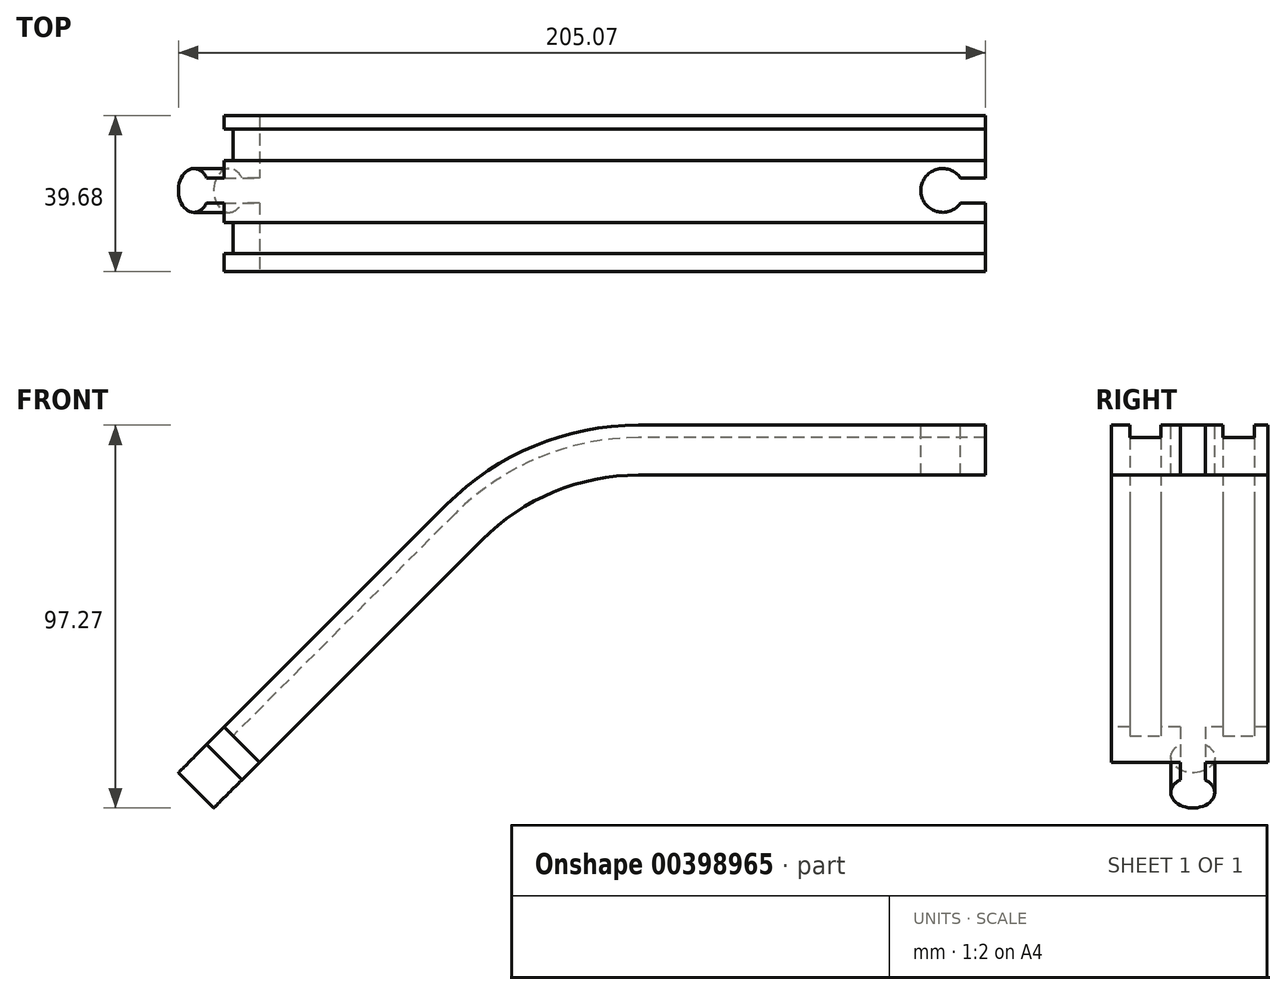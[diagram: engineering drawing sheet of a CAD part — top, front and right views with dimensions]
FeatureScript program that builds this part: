
annotation { "Feature Type Name" : "Feature", "Feature Type Description" : "" }
export const myFeature = defineFeature(function(context is Context, id is Id, definition is map)
    precondition{}
    {
        {
            var Q0;
            Q0=qCreatedBy(makeId("Right.planeOp"),FACE);
            var sketch = newSketch(context, id + "F0", { "sketchPlane" : qUnion([Q0])});
            skLineSegment(sketch, "E0.bottom", {"start": v(19.84, 6.35) * mm, "end": v(-19.84, 6.35) * mm});
            skLineSegment(sketch, "E0.top", {"start": v(19.84, -6.35) * mm, "end": v(-19.84, -6.35) * mm});
            skLineSegment(sketch, "E0.left", {"start": v(19.84, 6.35) * mm, "end": v(19.84, -6.35) * mm});
            skLineSegment(sketch, "E0.right", {"start": v(-19.84, 6.35) * mm, "end": v(-19.84, -6.35) * mm});
            skPoint(sketch, "E0.middle", {"position": v(0, 0) * mm});
            skSolve(sketch);
        }
        {
            var Q0;
            Q0=qCreatedBy(makeId("Front.planeOp"),FACE);
            var sketch = newSketch(context, id + "F1", { "sketchPlane" : qUnion([Q0])});
            skLineSegment(sketch, "E1", {"start": v(0, 0) * mm, "end": v(-88.25, 0) * mm});
            skArc(sketch, "E2", {"start": v(-88.25, 0) * mm, "mid": v(-112.17, -4.76) * mm, "end": v(-132.46, -18.31) * mm});
            skLineSegment(sketch, "E3", {"start": v(-132.46, -18.31) * mm, "end": v(-188.94, -74.79) * mm});
            skPoint(sketch, "E4", {"position": v(-132.46, -18.31) * mm});
            skSolve(sketch);
        }
        {
            var Q0;
            Q0 = qSketchRegion(id + "F0", true);
            var Q1;
            Q1 = qConstructionFilter(qBodyType(qCreatedBy(id + "F1" ,EDGE), BodyType.WIRE), ConstructionObject.NO);
            sweep(context, id + "F2", {"profiles" : qUnion([Q0]), "path" : qUnion([Q1])});
        }
        {
            var Q0;
            Q0=qCreatedBy(makeId("Top.planeOp"),FACE);
            var sketch = newSketch(context, id + "F3", { "sketchPlane" : qUnion([Q0])});
            skLineSegment(sketch, "E5.0", {"start": v(0, -19.84) * mm, "end": v(0, 19.84) * mm});
            skLineSegment(sketch, "E6", {"start": v(0, 3.97) * mm, "end": v(-6.35, 3.97) * mm});
            skLineSegment(sketch, "E7", {"start": v(0, -2.38) * mm, "end": v(-6.35, -2.38) * mm});
            skArc(sketch, "E8", {"start": v(-6.35, 3.97) * mm, "mid": v(-16.47, 0.8) * mm, "end": v(-6.35, -2.38) * mm});
            skSolve(sketch);
        }
        {
            var Q0;
            Q0 = qSketchRegion(id + "F3", true);
            extrude(context, id + "F4", {"entities" : qUnion([Q0]), "operationType" : NewBodyOperationType.REMOVE, "oppositeDirection" : true, "depth" : 25.4 * mm, "symmetric" : true});
        }
        {
            var Q0;
            Q0=makeQuery(id+"F2.opSweep","CAP_EDGE",EDGE,{"disambiguationData":[OSD([sQuery(id+"F0.wireOp",EDGE,"E0.right"),sQuery(id+"F1.wireOp",VERTEX,"E3.end")])],"isStart":false});
            cPoint(context, id + "F5", {"entities" : qUnion([Q0]), "parameter" : 0.5});
        }
        {
            var Q0;
            Q0=makeQuery(id+"F2.opSweep","SWEPT_FACE",FACE,{"disambiguationData":[OSD([sQuery(id+"F0.wireOp",EDGE,"E0.bottom"),sQuery(id+"F1.wireOp",EDGE,"E3")])]});
            var Q1;
            Q1 = qCreatedBy(id + "F5" ,VERTEX);
            cPlane(context, id + "F6", {"entities" : qUnion([Q0, Q1]), "cplaneType" : CPlaneType.PLANE_POINT, "offset" : 25.4 * mm, "width" : 152.4 * mm, "height" : 152.4 * mm});
        }
        {
            var Q0;
            Q0=qCreatedBy(id+"F6.planeOp",FACE);
            var sketch = newSketch(context, id + "F7", { "sketchPlane" : qUnion([Q0])});
            skLineSegment(sketch, "E9.0", {"start": v(19.84, -186.48) * mm, "end": v(-19.84, -186.48) * mm});
            skLineSegment(sketch, "E10", {"start": v(-3.97, -186.48) * mm, "end": v(-3.97, -192.83) * mm});
            skLineSegment(sketch, "E11", {"start": v(2.38, -186.48) * mm, "end": v(2.38, -192.83) * mm});
            skArc(sketch, "E12", {"start": v(-3.97, -192.83) * mm, "mid": v(-0.8, -202.95) * mm, "end": v(2.38, -192.83) * mm});
            skSolve(sketch);
        }
        {
            var Q0;
            Q0 = qSketchRegion(id + "F7", true);
            extrude(context, id + "F8", {"entities" : qUnion([Q0]), "operationType" : NewBodyOperationType.ADD, "depth" : 12.7 * mm, "symmetric" : true});
        }
        {
            var Q0;
            {var subQ1=sQuery(id+"F0.wireOp",EDGE,"E0.bottom");var subQ2=sQuery(id+"F0.wireOp",EDGE,"E0.top");var subQ3=sQuery(id+"F0.wireOp",EDGE,"E0.left");Q0=makeQuery(id+"F4.boolean.opBoolean","SPLIT",FACE,{"disambiguationData":[TD([makeQuery(id+"F4.opExtrude","SWEPT_FACE",FACE,{"disambiguationData":[OSD([sQuery(id+"F3.wireOp",EDGE,"E6")])]})])],"derivedFrom":makeQuery(id+"F2.opSweep","CAP_FACE",FACE,{"disambiguationData":[OSD([subQ1,subQ2,subQ3,sQuery(id+"F0.wireOp",EDGE,"E0.right"),sQuery(id+"F1.wireOp",VERTEX,"E1.start")])],"isStart":true})});}
            var sketch = newSketch(context, id + "F9", { "sketchPlane" : qUnion([Q0])});
            skLineSegment(sketch, "E13.bottom", {"start": v(8.45, 6.35) * mm, "end": v(16.39, 6.35) * mm});
            skLineSegment(sketch, "E13.top", {"start": v(8.45, 3.18) * mm, "end": v(16.39, 3.18) * mm});
            skLineSegment(sketch, "E13.left", {"start": v(8.45, 6.35) * mm, "end": v(8.45, 3.18) * mm});
            skLineSegment(sketch, "E13.right", {"start": v(16.39, 6.35) * mm, "end": v(16.39, 3.17) * mm});
            skSolve(sketch);
        }
        {
            var Q0;
            Q0 = qSketchRegion(id + "F9", true);
            var Q1;
            Q1 = qConstructionFilter(qBodyType(qCreatedBy(id + "F1" ,EDGE), BodyType.WIRE), ConstructionObject.NO);
            sweep(context, id + "F10", {"operationType" : NewBodyOperationType.REMOVE, "profiles" : qUnion([Q0]), "path" : qUnion([Q1])});
        }
        {
            var Q0;
            {var subQ1=sQuery(id+"F0.wireOp",EDGE,"E0.bottom");var subQ2=sQuery(id+"F0.wireOp",EDGE,"E0.top");var subQ3=sQuery(id+"F0.wireOp",EDGE,"E0.right");Q0=makeQuery(id+"F4.boolean.opBoolean","SPLIT",FACE,{"disambiguationData":[TD([makeQuery(id+"F4.opExtrude","SWEPT_FACE",FACE,{"disambiguationData":[OSD([sQuery(id+"F3.wireOp",EDGE,"E7")])]})])],"derivedFrom":makeQuery(id+"F2.opSweep","CAP_FACE",FACE,{"disambiguationData":[OSD([subQ1,subQ2,sQuery(id+"F0.wireOp",EDGE,"E0.left"),subQ3,sQuery(id+"F1.wireOp",VERTEX,"E1.start")])],"isStart":true})});}
            var sketch = newSketch(context, id + "F11", { "sketchPlane" : qUnion([Q0])});
            skLineSegment(sketch, "E14.bottom", {"start": v(-15.24, 6.35) * mm, "end": v(-7.3, 6.35) * mm});
            skLineSegment(sketch, "E14.top", {"start": v(-15.24, 3.18) * mm, "end": v(-7.3, 3.18) * mm});
            skLineSegment(sketch, "E14.left", {"start": v(-15.24, 6.35) * mm, "end": v(-15.24, 3.18) * mm});
            skLineSegment(sketch, "E14.right", {"start": v(-7.3, 6.35) * mm, "end": v(-7.3, 3.18) * mm});
            skSolve(sketch);
        }
        {
            var Q0;
            Q0 = qSketchRegion(id + "F11", true);
            var Q1;
            Q1 = qConstructionFilter(qBodyType(qCreatedBy(id + "F1" ,EDGE), BodyType.WIRE), ConstructionObject.NO);
            sweep(context, id + "F12", {"operationType" : NewBodyOperationType.REMOVE, "profiles" : qUnion([Q0]), "path" : qUnion([Q1])});
        }
    });
